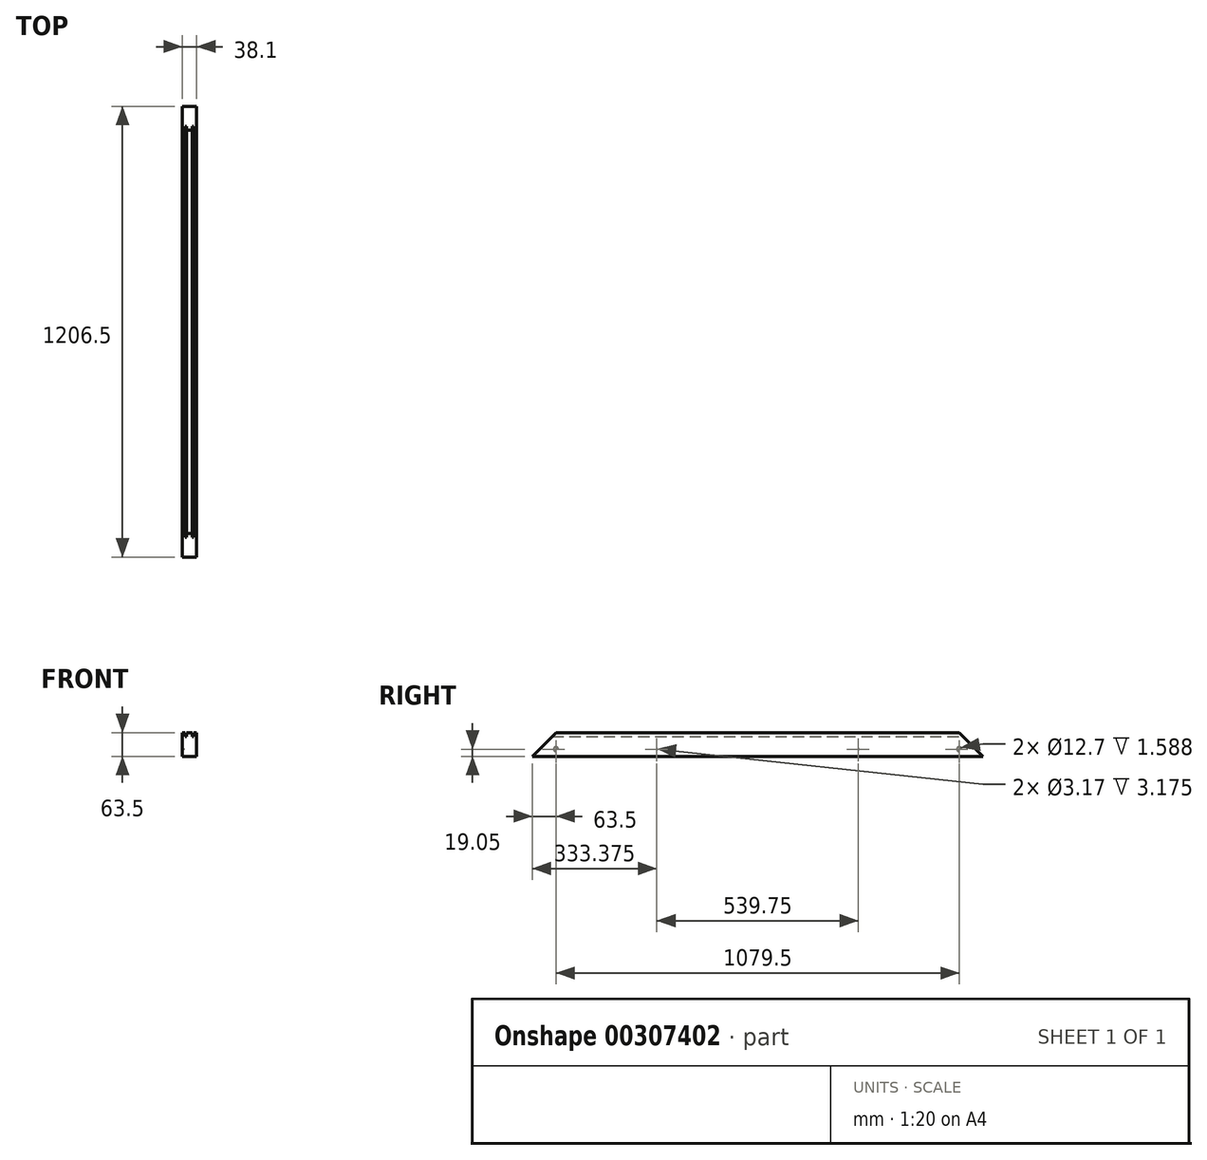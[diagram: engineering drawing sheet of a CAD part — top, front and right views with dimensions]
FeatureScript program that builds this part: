
annotation { "Feature Type Name" : "Feature", "Feature Type Description" : "" }
export const myFeature = defineFeature(function(context is Context, id is Id, definition is map)
    precondition{}
    {
        {
            var Q0;
            Q0=qCreatedBy(makeId("Front.planeOp"),FACE);
            var sketch = newSketch(context, id + "F0", { "sketchPlane" : qUnion([Q0])});
            skLineSegment(sketch, "E0.bottom", {"start": v(19.05, -31.75) * mm, "end": v(-19.05, -31.75) * mm});
            skLineSegment(sketch, "E0.top", {"start": v(19.05, 31.75) * mm, "end": v(-19.05, 31.75) * mm});
            skLineSegment(sketch, "E0.left", {"start": v(19.05, -31.75) * mm, "end": v(19.05, 31.75) * mm});
            skLineSegment(sketch, "E0.right", {"start": v(-19.05, -31.75) * mm, "end": v(-19.05, 31.75) * mm});
            skPoint(sketch, "E0.middle", {"position": v(0, 0) * mm});
            skLineSegment(sketch, "E1.bottom", {"start": v(11.11, 21.59) * mm, "end": v(7.94, 21.59) * mm});
            skLineSegment(sketch, "E1.top", {"start": v(11.11, 31.75) * mm, "end": v(7.94, 31.75) * mm});
            skLineSegment(sketch, "E1.left", {"start": v(11.11, 21.59) * mm, "end": v(11.11, 31.75) * mm});
            skLineSegment(sketch, "E1.right", {"start": v(7.94, 21.59) * mm, "end": v(7.94, 31.75) * mm});
            skPoint(sketch, "E1.middle", {"position": v(9.53, 26.67) * mm});
            skLineSegment(sketch, "E2.bottom", {"start": v(-7.94, 21.59) * mm, "end": v(-11.11, 21.59) * mm});
            skLineSegment(sketch, "E2.top", {"start": v(-7.94, 31.75) * mm, "end": v(-11.11, 31.75) * mm});
            skLineSegment(sketch, "E2.left", {"start": v(-7.94, 21.59) * mm, "end": v(-7.94, 31.75) * mm});
            skLineSegment(sketch, "E2.right", {"start": v(-11.11, 21.59) * mm, "end": v(-11.11, 31.75) * mm});
            skPoint(sketch, "E2.middle", {"position": v(-9.53, 26.67) * mm});
            skSolve(sketch);
        }
        {
            var Q0;
            Q0=makeQuery(id+"F0.imprint","IMPRINT",FACE,{"disambiguationData":[TD([[makeQuery(id+"F0.imprint","IMPRINT",EDGE,{"derivedFrom":sQuery(id+"F0.wireOp",EDGE,"E0.bottom")}),-1.0]])]});
            extrude(context, id + "F1", {"entities" : qUnion([Q0]), "endBound" : BoundingType.SYMMETRIC, "depth" : 1206.5 * mm});
        }
        {
            var Q0;
            Q0=makeQuery(id+"F1.opExtrude","SWEPT_FACE",FACE,{"disambiguationData":[OSD([sQuery(id+"F0.wireOp",EDGE,"E0.right")])]});
            var sketch = newSketch(context, id + "F2", { "sketchPlane" : qUnion([Q0])});
            skLineSegment(sketch, "E3", {"start": v(603.25, -31.75) * mm, "end": v(539.75, 31.75) * mm});
            skLineSegment(sketch, "E4", {"start": v(539.75, 31.75) * mm, "end": v(603.25, 31.75) * mm});
            skLineSegment(sketch, "E5", {"start": v(603.25, 31.75) * mm, "end": v(603.25, -31.75) * mm});
            skLineSegment(sketch, "E6", {"start": v(-603.25, -31.75) * mm, "end": v(-539.75, 31.75) * mm});
            skLineSegment(sketch, "E7", {"start": v(-539.75, 31.75) * mm, "end": v(-603.25, 31.75) * mm});
            skLineSegment(sketch, "E8", {"start": v(-603.25, 31.75) * mm, "end": v(-603.25, -31.75) * mm});
            skSolve(sketch);
        }
        {
            var Q0;
            Q0=qSketchRegion(id+"F2",true);
            extrude(context, id + "F3", {"entities" : qUnion([Q0]), "operationType" : NewBodyOperationType.REMOVE, "endBound" : BoundingType.THROUGH_ALL, "oppositeDirection" : true, "depth" : 25.4 * mm});
        }
        {
            var Q0;
            {var subQ0=sQuery(id+"F2.wireOp",EDGE,"E3");Q0=makeQuery(id+"F2.imprint","IMPRINT",FACE,{"disambiguationData":[TD([[makeQuery(id+"F2.imprint","IMPRINT",EDGE,{"derivedFrom":subQ0}),1.0]])]});}
            var sketch = newSketch(context, id + "F4", { "sketchPlane" : qUnion([Q0])});
            skCircle(sketch, "E9", {"center": v(539.75, -12.7) * mm, "radius": 6.35 * mm});
            skCircle(sketch, "E10", {"center": v(-539.75, -12.7) * mm, "radius": 6.35 * mm});
            skSolve(sketch);
        }
        {
            var Q0;
            Q0 = qSketchRegion(id + "F4", true);
            extrude(context, id + "F5", {"entities" : qUnion([Q0]), "operationType" : NewBodyOperationType.REMOVE, "oppositeDirection" : true, "depth" : 1.59 * mm});
        }
        {
            var Q0;
            {var subQ0=sQuery(id+"F2.wireOp",EDGE,"E3");Q0=makeQuery(id+"F2.imprint","IMPRINT",FACE,{"disambiguationData":[TD([[makeQuery(id+"F2.imprint","IMPRINT",EDGE,{"derivedFrom":subQ0}),1.0]])]});}
            var sketch = newSketch(context, id + "F6", { "sketchPlane" : qUnion([Q0])});
            skCircle(sketch, "E11", {"center": v(269.88, -12.7) * mm, "radius": 1.59 * mm});
            skCircle(sketch, "E12", {"center": v(-269.88, -12.7) * mm, "radius": 1.59 * mm});
            skLineSegment(sketch, "E13", {"start": v(0, -12.7) * mm, "end": v(269.88, -12.7) * mm, "construction": true});
            skLineSegment(sketch, "E14", {"start": v(539.75, -12.7) * mm, "end": v(269.88, -12.7) * mm, "construction": true});
            skCircle(sketch, "E15.0", {"center": v(539.75, -12.7) * mm, "radius": 6.35 * mm, "construction": true});
            skSolve(sketch);
        }
        {
            var Q0;
            Q0 = qSketchRegion(id + "F6", true);
            extrude(context, id + "F7", {"entities" : qUnion([Q0]), "operationType" : NewBodyOperationType.REMOVE, "oppositeDirection" : true, "depth" : 3.17 * mm});
        }
    });
